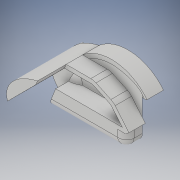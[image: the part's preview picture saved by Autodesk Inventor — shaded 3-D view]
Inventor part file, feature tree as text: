
AUTODESK INVENTOR PART (.ipt)
format: ipt  version: 2017 (Build 210142000, 142)  size: 568,832 bytes
history: native  units: mm
features: sketch x26, extrude x22, plane x7, fillet x4, other x3, revolve x1, boolean_combine x1
ambient origin geometry x8: Origin, YZ Plane, XZ Plane, XY Plane, X Axis, Y Axis, Z Axis, Center Point
bodies: Solid1 (feature_tree), Solid2 (feature_tree)
feature tree (64):
  extrude  "Extrusion1"  Depth=60.0mm
  plane  "Work Plane1"
  extrude  "Extrusion2"  Depth=60.0mm
  other  "Bend Part1"
  other  "Bend Part2"
  extrude  "Extrusion3"  Depth=32.454mm
  plane  "Work Plane2"
  extrude  "Extrusion4"  Depth=20.0mm
  other  "Bend Part3"
  extrude  "Extrusion5"  Depth=30.0mm
  revolve  "Revolution1"  [1 undecoded]
  plane  "Work Plane3"
  extrude  "Extrusion6"  Depth=10.0mm
  boolean_combine  "Combine1"
  plane  "Work Plane4"
  extrude  "Extrusion7"  TaperAngle=90.0deg  [1 undecoded]
  extrude  "Extrusion8"  Depth=80.0mm
  extrude  "Extrusion9"  Depth=50.0mm TaperAngle=135.0deg
  extrude  "Extrusion10"  Depth=60.0mm
  plane  "Work Plane5"
  extrude  "Extrusion11"  Depth=60.0mm
  extrude  "Extrusion12"  Depth=60.0mm
  plane  "Work Plane6"
  extrude  "Extrusion13"  [1 undecoded]
  extrude  "Extrusion14"  Depth=30.0mm TaperAngle=0.0deg
  plane  "Work Plane7"
  extrude  "Extrusion15"  Depth=20.0mm TaperAngle=0.0deg
  extrude  "Extrusion16"  Depth=15.219936mm
  extrude  "Extrusion17"  Depth=15.155142mm
  fillet  "Fillet1"  Radius=20.0mm
  extrude  "Extrusion18"  Depth=60.0mm
  fillet  "Fillet2"  Radius=43.193283mm
  fillet  "Fillet3"  Radius=60.0mm
  fillet  "Fillet4"  Radius=60.5mm
  extrude  "Extrusion19"  Depth=25.287025mm
  extrude  "Extrusion20"  Depth=2.439mm TaperAngle=0.0deg
  extrude  "Extrusion21"  Depth=0.980484mm
  extrude  "Extrusion22"  Depth=2.246206mm
  sketch  "Sketch1"  dims[d0=60.0mm d1=35.0mm]
  sketch  "Sketch2"  dims[d2=60.0mm d3=33.005006mm]
  sketch  "Sketch3"  dims[d4=75.0mm d5=0.0mm d6=32.454mm]
  sketch  "Sketch4"  dims[d7=85.0mm d8=20.0mm]
  sketch  "Sketch5"  dims[d9=5.0mm d10=0.0mm d11=30.0mm]
  sketch  "Sketch6"  dims[d12=55.0mm d13=10.0mm d14=4.363323mm]
  sketch  "Sketch7"  dims[d15=20.0mm d16=10.0mm d17=4.363323mm]
  sketch  "Sketch8"  dims[d18=20.0mm d19=0.0mm d20=90.0deg]
  sketch  "Sketch9"  dims[d21=20.0mm d22=80.0mm]
  sketch  "Sketch10"  dims[d23=5.0mm d24=0.0mm d25=50.0mm d26=135.0deg]
  sketch  "Sketch11"  dims[d27=60.0mm d28=35.0mm]
  sketch  "Sketch12"  dims[d29=35.0mm d30=60.0mm]
  sketch  "Sketch13"  dims[d31=20.0mm d32=0.0mm d33=60.0mm]
  sketch  "Sketch14"  dims[d34=270.0deg d35=-4.697mm]
  sketch  "Sketch15"  dims[d36=20.0mm d37=30.0mm d38=0.0mm]
  sketch  "Sketch16"  dims[d39=-20.0mm d40=20.0mm d41=0.0mm]
  sketch  "Sketch17"  dims[d42=35.67mm d43=15.219936mm]
  sketch  "Sketch18"  dims[d44=35.67mm d45=15.155142mm d46=20.0mm d47=0.0mm]
  sketch  "Sketch19"  dims[d48=20.0mm d49=0.0mm d50=100.334153mm d51=43.193283mm d52=60.0mm d53=0.0mm d54=60.5mm]
  sketch  "Sketch20"  dims[d55=14.497104mm d56=25.287025mm]
  sketch  "Sketch21"  dims[d57=104.0mm d58=0.0mm d59=2.439mm d60=0.0mm]
  sketch  "Sketch22"  dims[d61=-31.25mm d62=0.980484mm]
  sketch  "Sketch23"  dims[d63=1.164325mm d64=2.246206mm]
  sketch  "Sketch24"  dims[d65=25.536883mm]
  sketch  "Sketch25"  dims[d66=100.0mm d67=0.0mm]
  sketch  "Sketch26"  dims[d68=0.0mm d69=5.0mm d70=0.0mm d71=50.209mm d72=95.197mm d73=0.0mm d74=95.197mm d75=0.0mm d76=60.0mm d77=60.0mm d78=20.0mm d79=18.461mm d80=116.447mm d81=0.0mm d82=10.0mm d83=8.797686mm d84=116.447mm d85=0.0mm d86=10.0mm d87=9.0mm d88=10.0mm d89=60.197145mm d90=34.482005mm d91=20.0mm d92=3.0mm d93=20.0mm d94=90.0deg d95=55.512917mm d96=23.386841mm d97=11.976391mm d98=75.0mm d99=0.0mm d100=3.0mm d101=20.0mm d102=75.0mm d103=0.0mm d104=14.0mm d105=2.0mm d106=75.0mm d107=0.0mm d108=20.0mm d109=60.0mm d110=10.0mm d111=0.0mm]
note: 3 required parameter values undecoded (feature->parameter linkage not recoverable at this tier; creation-order binding heuristic only, values carry confidence <= 0.55)